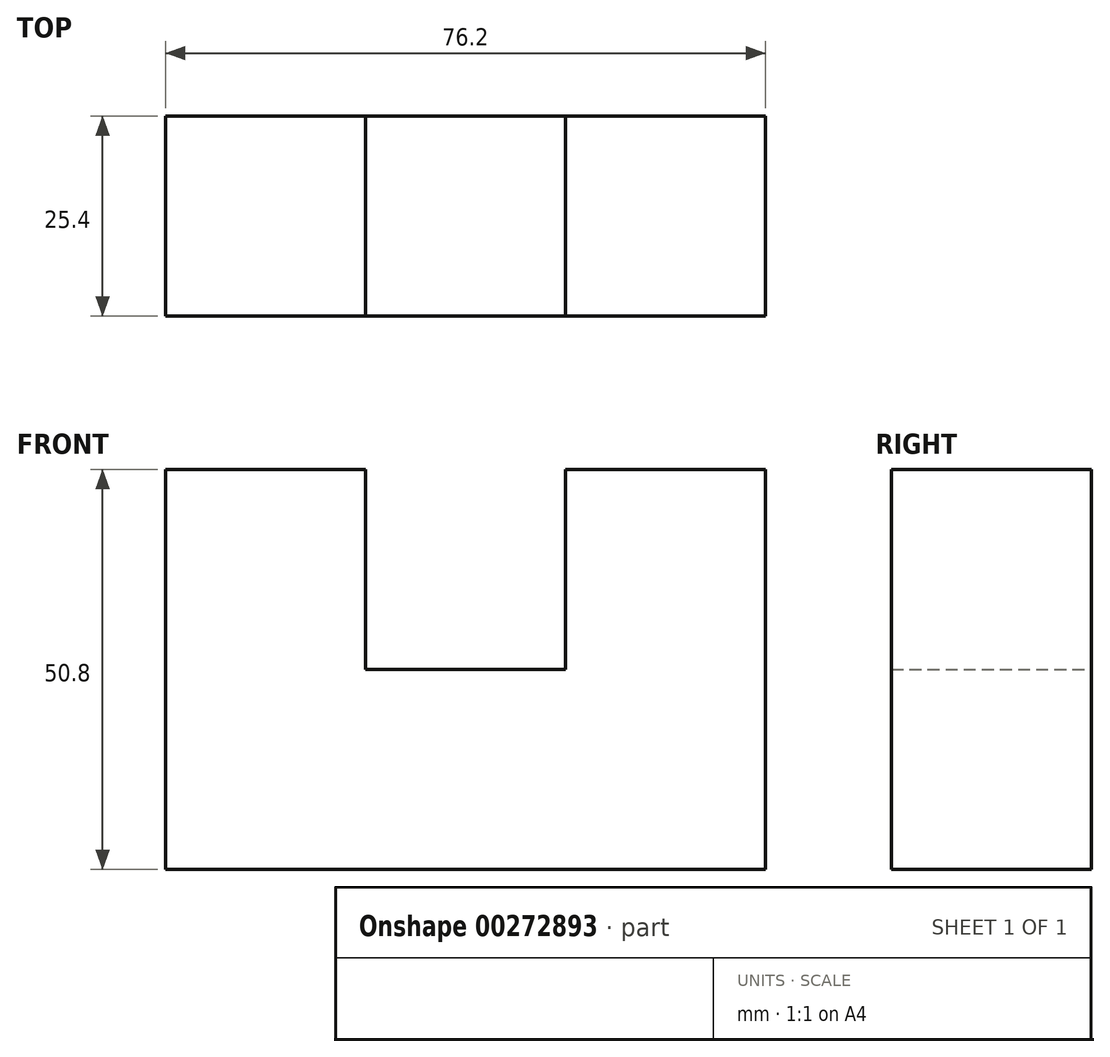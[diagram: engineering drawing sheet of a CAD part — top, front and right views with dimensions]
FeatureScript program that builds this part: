
annotation { "Feature Type Name" : "Feature", "Feature Type Description" : "" }
export const myFeature = defineFeature(function(context is Context, id is Id, definition is map)
    precondition{}
    {
        {
            var Q0;
            Q0=qCreatedBy(makeId("Front.planeOp"),FACE);
            var sketch = newSketch(context, id + "F0", { "sketchPlane" : qUnion([Q0])});
            skLineSegment(sketch, "E0", {"start": v(0, 0) * mm, "end": v(-76.2, 0) * mm});
            skLineSegment(sketch, "E1", {"start": v(-76.2, 50.8) * mm, "end": v(-76.2, 0) * mm});
            skLineSegment(sketch, "E2", {"start": v(-76.2, 50.8) * mm, "end": v(-50.8, 50.8) * mm});
            skLineSegment(sketch, "E3", {"start": v(-50.8, 25.4) * mm, "end": v(-50.8, 50.8) * mm});
            skLineSegment(sketch, "E4", {"start": v(-50.8, 25.4) * mm, "end": v(-25.4, 25.4) * mm});
            skLineSegment(sketch, "E5", {"start": v(-25.4, 50.8) * mm, "end": v(-25.4, 25.4) * mm});
            skLineSegment(sketch, "E6", {"start": v(-25.4, 50.8) * mm, "end": v(0, 50.8) * mm});
            skLineSegment(sketch, "E7", {"start": v(0, 0) * mm, "end": v(0, 50.8) * mm});
            skSolve(sketch);
        }
        {
            var Q0;
            Q0=makeQuery(id+"F0.imprint","IMPRINT",FACE,{"disambiguationData":[TD([[makeQuery(id+"F0.imprint","IMPRINT",EDGE,{"derivedFrom":sQuery(id+"F0.wireOp",EDGE,"E0")}),-1.0]])]});
            extrude(context, id + "F1", {"entities" : qUnion([Q0]), "depth" : 25.4 * mm});
        }
    });
